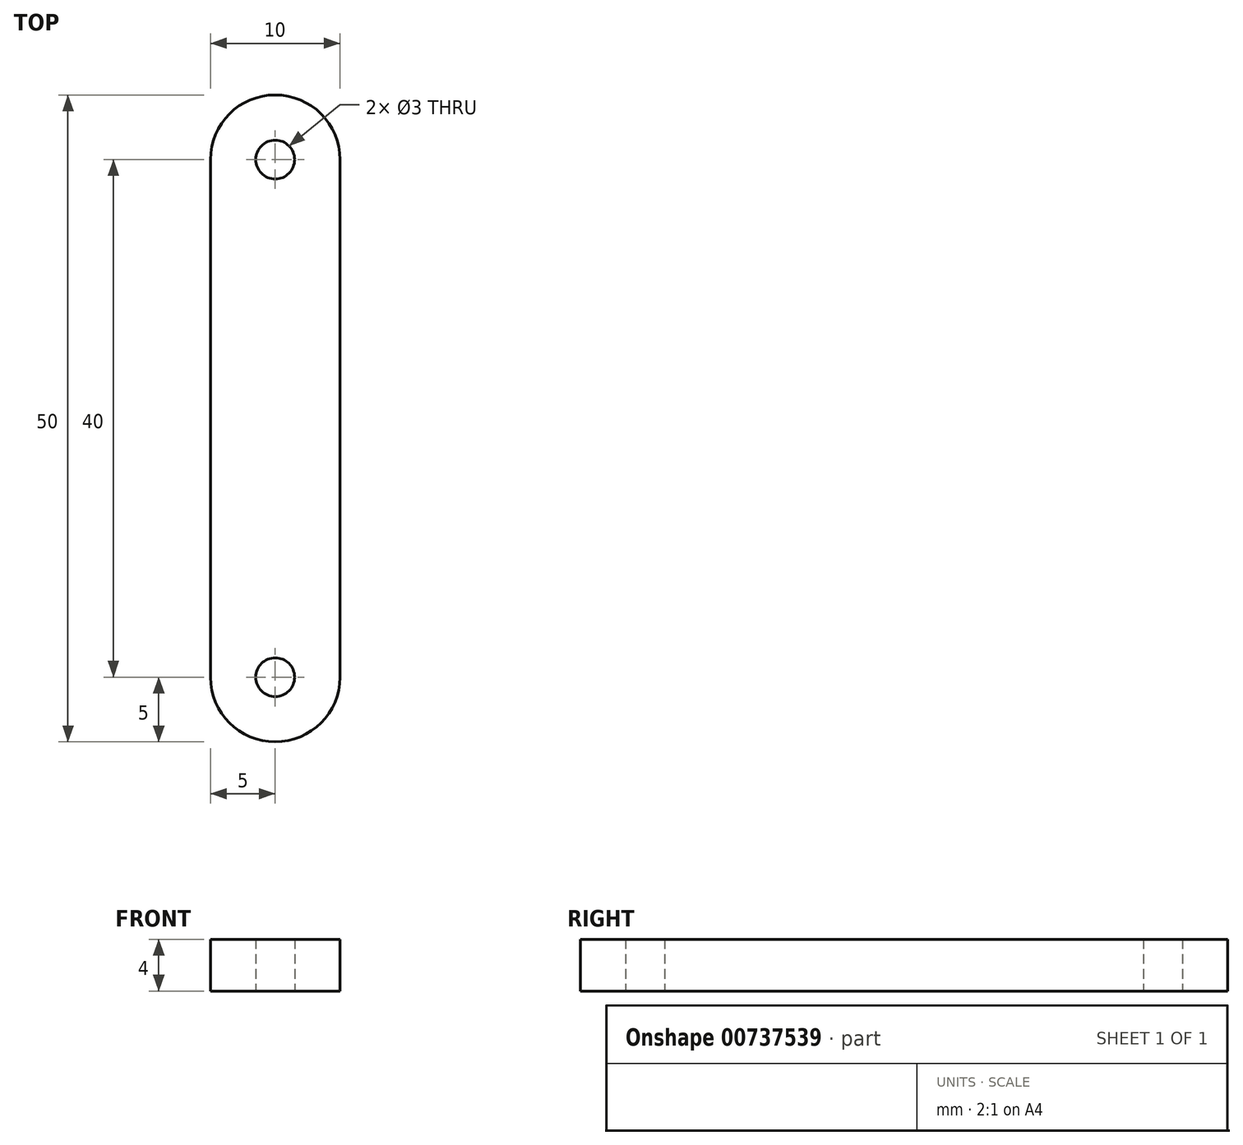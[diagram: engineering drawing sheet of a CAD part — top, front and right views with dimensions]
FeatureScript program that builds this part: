
annotation { "Feature Type Name" : "Feature", "Feature Type Description" : "" }
export const myFeature = defineFeature(function(context is Context, id is Id, definition is map)
    precondition{}
    {
        {
            var Q0;
            Q0=qCreatedBy(makeId("Top.planeOp"),FACE);
            var sketch = newSketch(context, id + "F0", { "sketchPlane" : qUnion([Q0])});
            skCircle(sketch, "E0", {"center": v(0, 23.96) * mm, "radius": 5 * mm});
            skCircle(sketch, "E1", {"center": v(0, -16.04) * mm, "radius": 5 * mm});
            skLineSegment(sketch, "E2", {"start": v(-5, 23.96) * mm, "end": v(-5, -16.04) * mm});
            skLineSegment(sketch, "E3", {"start": v(5, 23.96) * mm, "end": v(5, -16.04) * mm});
            skCircle(sketch, "E4", {"center": v(0, 23.96) * mm, "radius": 1.5 * mm});
            skCircle(sketch, "E5", {"center": v(0, -16.04) * mm, "radius": 1.5 * mm});
            skSolve(sketch);
        }
        {
            var Q0;
            Q0=makeQuery(id+"F0.imprint","IMPRINT",FACE,{"disambiguationData":[TD([[makeQuery(id+"F0.imprint","IMPRINT",EDGE,{"derivedFrom":sQuery(id+"F0.wireOp",EDGE,"E4")}),-1.0]])]});
            var Q1;
            {var subQ0=sQuery(id+"F0.wireOp",EDGE,"E2");Q1=makeQuery(id+"F0.imprint","IMPRINT",FACE,{"disambiguationData":[TD([[makeQuery(id+"F0.imprint","IMPRINT",EDGE,{"derivedFrom":subQ0}),1.0]])]});}
            var Q2;
            Q2=makeQuery(id+"F0.imprint","IMPRINT",FACE,{"disambiguationData":[TD([[makeQuery(id+"F0.imprint","IMPRINT",EDGE,{"derivedFrom":sQuery(id+"F0.wireOp",EDGE,"E5")}),-1.0]])]});
            extrude(context, id + "F1", {"entities" : qUnion([Q0, Q1, Q2]), "depth" : 4 * mm, "offsetDistance" : 25 * mm});
        }
    });
